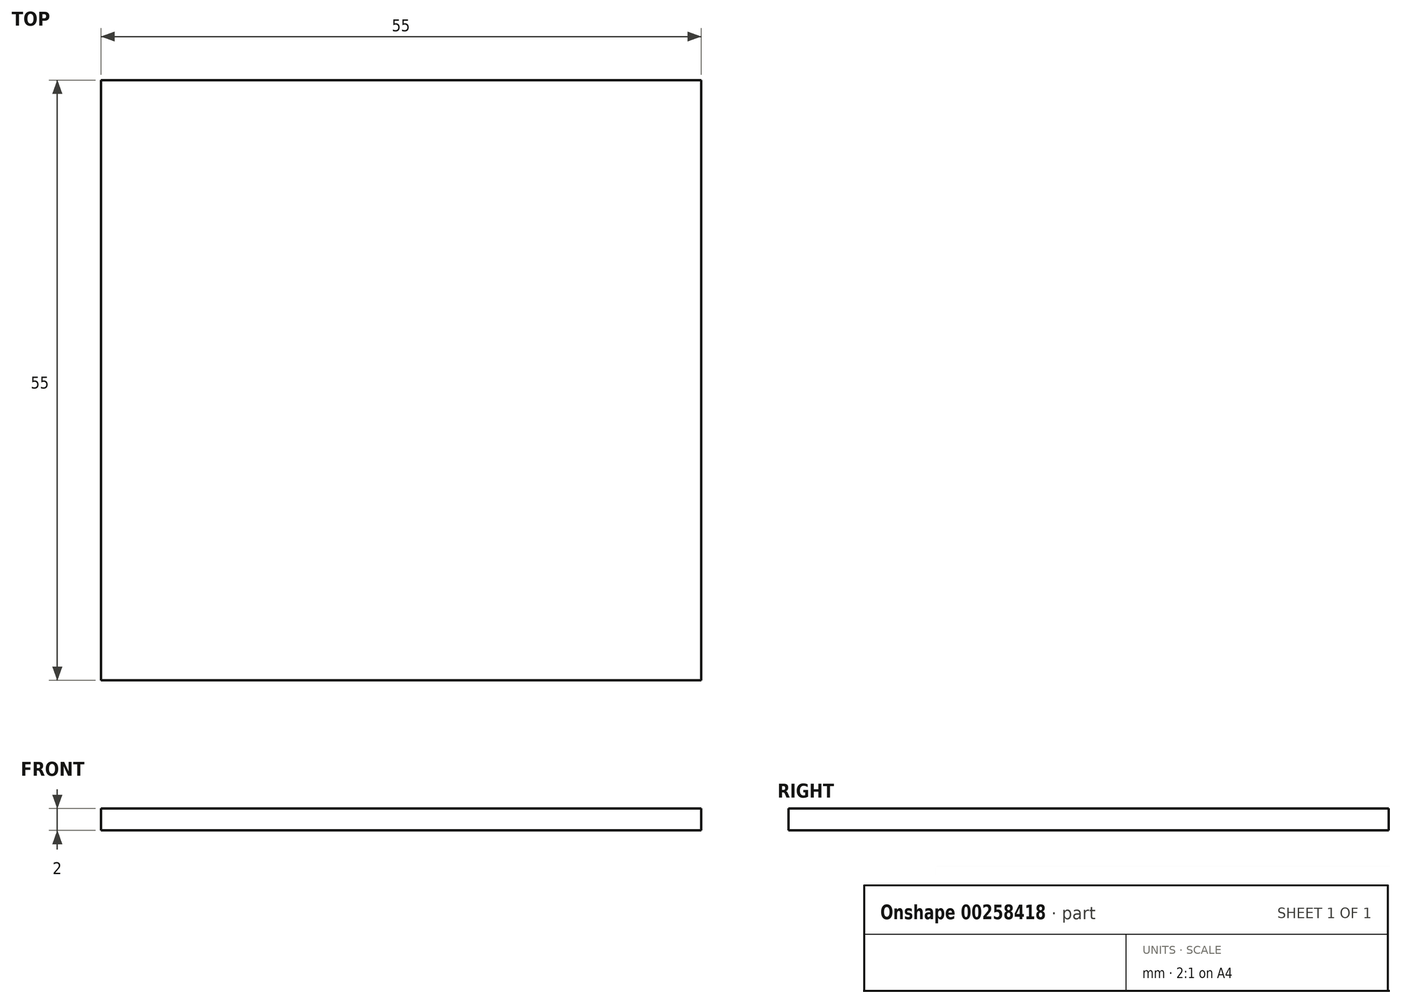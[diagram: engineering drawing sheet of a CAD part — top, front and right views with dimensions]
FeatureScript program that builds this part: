
annotation { "Feature Type Name" : "Feature", "Feature Type Description" : "" }
export const myFeature = defineFeature(function(context is Context, id is Id, definition is map)
    precondition{}
    {
        {
            var Q0;
            Q0=qCreatedBy(makeId("Top.planeOp"),FACE);
            var sketch = newSketch(context, id + "F0", { "sketchPlane" : qUnion([Q0])});
            skLineSegment(sketch, "E0.bottom", {"start": v(27.5, -27.5) * mm, "end": v(-27.5, -27.5) * mm});
            skLineSegment(sketch, "E0.top", {"start": v(27.5, 27.5) * mm, "end": v(-27.5, 27.5) * mm});
            skLineSegment(sketch, "E0.left", {"start": v(27.5, -27.5) * mm, "end": v(27.5, 27.5) * mm});
            skLineSegment(sketch, "E0.right", {"start": v(-27.5, -27.5) * mm, "end": v(-27.5, 27.5) * mm});
            skPoint(sketch, "E0.middle", {"position": v(0, 0) * mm});
            skSolve(sketch);
        }
        {
            var Q0;
            Q0=makeQuery(id+"F0.imprint","IMPRINT",FACE,{"disambiguationData":[TD([[makeQuery(id+"F0.imprint","IMPRINT",EDGE,{"derivedFrom":sQuery(id+"F0.wireOp",EDGE,"E0.bottom")}),-1.0]])]});
            extrude(context, id + "F1", {"entities" : qUnion([Q0]), "depth" : 2 * mm});
        }
    });
